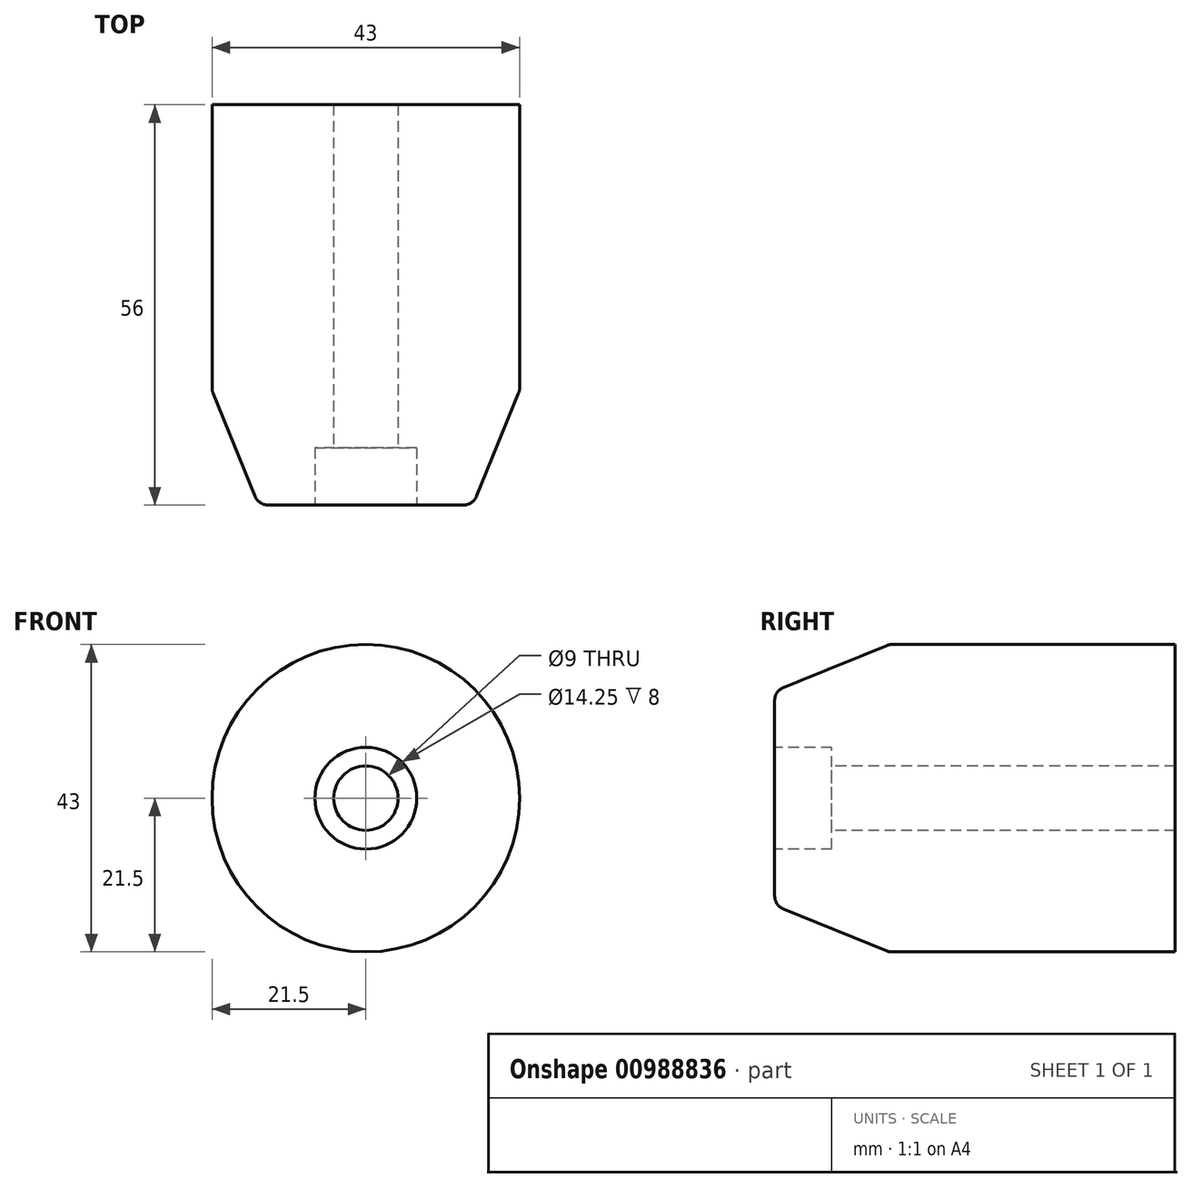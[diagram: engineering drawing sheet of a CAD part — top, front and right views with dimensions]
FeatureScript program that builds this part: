
annotation { "Feature Type Name" : "Feature", "Feature Type Description" : "" }
export const myFeature = defineFeature(function(context is Context, id is Id, definition is map)
    precondition{}
    {
        {
            var Q0;
            Q0=qCreatedBy(makeId("Front.planeOp"),FACE);
            var sketch = newSketch(context, id + "F0", { "sketchPlane" : qUnion([Q0])});
            skCircle(sketch, "E0", {"center": v(0, 0) * mm, "radius": 21.5 * mm});
            skSolve(sketch);
        }
        {
            var Q0;
            Q0 = qSketchRegion(id + "F0", true);
            extrude(context, id + "F1", {"entities" : qUnion([Q0]), "depth" : 40 * mm, "offsetDistance" : 25 * mm});
        }
        {
            var Q0;
            Q0=qCreatedBy(makeId("Front.planeOp"),FACE);
            cPlane(context, id + "F2", {"entities" : qUnion([Q0]), "cplaneType" : CPlaneType.OFFSET, "offset" : 56 * mm, "width" : 150 * mm, "height" : 150 * mm});
        }
        {
            var Q0;
            Q0=qCreatedBy(id+"F2.planeOp",FACE);
            var sketch = newSketch(context, id + "F3", { "sketchPlane" : qUnion([Q0])});
            skCircle(sketch, "E1", {"center": v(0, 0) * mm, "radius": 15 * mm});
            skSolve(sketch);
        }
        {
            var Q1;
            Q1=makeQuery(id+"F3.imprint","IMPRINT",FACE,{"disambiguationData":[TD([[makeQuery(id+"F3.imprint","IMPRINT",EDGE,{"derivedFrom":sQuery(id+"F3.wireOp",EDGE,"E1")}),1.0]])]});
            var Q2;
            Q2=makeQuery(id+"F1.opExtrude","CAP_FACE",FACE,{"disambiguationData":[OSD([sQuery(id+"F0.wireOp",EDGE,"E0")])],"isStart":false});
            loft(context, id + "F4", {"operationType" : NewBodyOperationType.ADD, "sheetProfilesArray" : [{ "sheetProfileEntities" : qUnion([Q1]) }, { "sheetProfileEntities" : qUnion([Q2]) }]});
        }
        {
            var Q0;
            Q0=qCreatedBy(id+"F2.planeOp",FACE);
            var sketch = newSketch(context, id + "F5", { "sketchPlane" : qUnion([Q0])});
            skPoint(sketch, "E2", {"position": v(0, 0) * mm});
            skSolve(sketch);
        }
        {
            var Q0;
            Q0=sQuery(id+"F5.wireOp",VERTEX,"E2");
            var Q1;
            Q1=makeQuery(id+"F1.opExtrude","SWEPT_BODY",BODY,{"disambiguationData":[OSD([sQuery(id+"F0.wireOp",EDGE,"E0")])]});
            hole(context, id + "F6", {"style" : HoleStyle.C_BORE, "endStyle" : HoleEndStyle.THROUGH, "standardTappedOrClearance" : lookupTablePath({ "fit" : "Normal", "standard" : "ISO", "size" : "M8", "type" : "Clearance" }), "standardBlindInLast" : lookupTablePath({ "fit" : "Normal", "standard" : "ISO", "engagement" : "75%", "pitch" : "1.25 mm", "size" : "M8", "type" : "Clearance & tapped" }), "holeDiameter" : 9 * mm, "cBoreDiameter" : 14.25 * mm, "cBoreDepth" : 8 * mm, "majorDiameter" : 5 * mm, "isTappedThrough" : true, "tappedDepth" : 5.6 * mm, "tapClearance" : 3, "startFromSketch" : true, "locations" : qUnion([Q0]), "scope" : qUnion([Q1])});
        }
        {
            var Q0;
            {var subQ0=sQuery(id+"F0.wireOp",EDGE,"E0");Q0=makeQuery(id+"F4.boolean.opBoolean","MERGE",EDGE,{"derivedFrom":[makeQuery(id+"F1.opExtrude","CAP_EDGE",EDGE,{"disambiguationData":[OSD([subQ0])],"isStart":false}),makeQuery(id+"F4.opLoft","MID_CAP_EDGE",EDGE,{"disambiguationData":[OSD([subQ0])],"capPos":1.0})]});}
            var Q1;
            Q1=makeQuery(id+"F4.opLoft","MID_CAP_EDGE",EDGE,{"disambiguationData":[OSD([sQuery(id+"F3.wireOp",EDGE,"E1")])],"capPos":0.0});
            fillet(context, id + "F7", {"entities" : qUnion([Q0, Q1]), "radius" : 2 * mm, "tangentPropagation" : true, "allowEdgeOverflow" : false});
        }
    });
